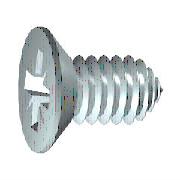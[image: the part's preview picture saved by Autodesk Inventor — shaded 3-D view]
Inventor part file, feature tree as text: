
AUTODESK INVENTOR PART (.ipt)
format: ipt  version: 2020 (Build 240168000, 168)  size: 269,312 bytes
history: native  units: mm (DEFAULTED — no unit token found)
features: extrude x2, plane x1, sketch x1
ambient origin geometry x8: Origin, YZ Plane, XZ Plane, XY Plane, X Axis, Y Axis, Z Axis, Center Point
bodies: Solid1 (feature_tree), Body (feature_tree)
feature tree (4):
  extrude  "Slot"  TaperAngle=45.0deg  [1 undecoded]
  extrude  "Star Cut"  Depth=2.05mm
  plane  "Work Plane2"
  sketch  "Sketch3"  dims[d0=22.0mm d2=45.0deg d3=3.5mm d5=7.3mm d6=4.1mm d7=4.625123mm d8=10.821041mm d9=2.2mm d16=90.0deg d10=45.0deg d11=1.64mm d12=4.1mm d13=0.515mm d14=4.1mm d15=45.0deg d17=0.515mm d18=2.35mm d19=-5.235988mm d20=19.65mm d21=0.0mm d22=1.75mm d23=3.2mm d25=0.0mm d26=2.05mm d66=25.4mm d27=0.872665mm d28=0.206mm d29=2.35mm d71=45.0deg d73=0.0mm d74=0.0mm]
note: 1 required parameter value undecoded (feature->parameter linkage not recoverable at this tier; creation-order binding heuristic only, values carry confidence <= 0.55)
